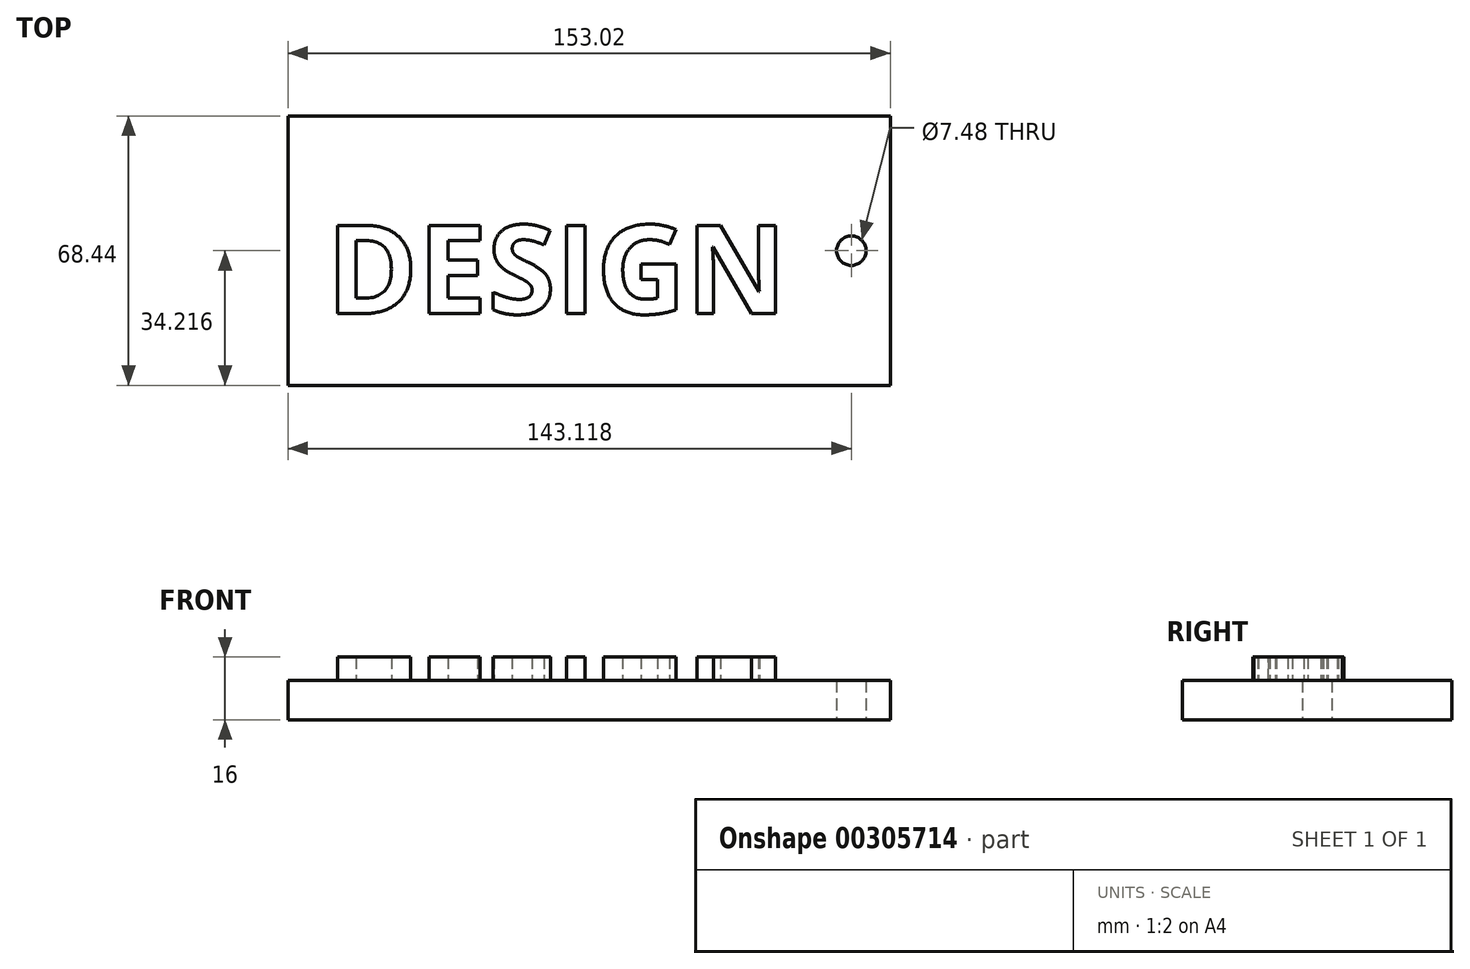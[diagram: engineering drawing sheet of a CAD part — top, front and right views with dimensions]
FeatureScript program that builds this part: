
annotation { "Feature Type Name" : "Feature", "Feature Type Description" : "" }
export const myFeature = defineFeature(function(context is Context, id is Id, definition is map)
    precondition{}
    {
        {
            var Q0;
            Q0=qCreatedBy(makeId("Top.planeOp"),FACE);
            var sketch = newSketch(context, id + "F0", { "sketchPlane" : qUnion([Q0])});
            skLineSegment(sketch, "E0.bottom", {"start": v(-119.97, 50.22) * mm, "end": v(33.05, 50.22) * mm});
            skLineSegment(sketch, "E0.top", {"start": v(-119.97, -18.22) * mm, "end": v(33.05, -18.22) * mm});
            skLineSegment(sketch, "E0.left", {"start": v(-119.97, 50.22) * mm, "end": v(-119.97, -18.22) * mm});
            skLineSegment(sketch, "E0.right", {"start": v(33.05, 50.22) * mm, "end": v(33.05, -18.22) * mm});
            skPoint(sketch, "E1.centerSnap0", {"position": v(33.05, 16) * mm});
            skCircle(sketch, "E2", {"center": v(23.15, 16) * mm, "radius": 3.74 * mm});
            skSolve(sketch);
        }
        {
            var Q0;
            Q0=makeQuery(id+"F0.imprint","IMPRINT",FACE,{"disambiguationData":[TD([[makeQuery(id+"F0.imprint","IMPRINT",EDGE,{"derivedFrom":sQuery(id+"F0.wireOp",EDGE,"E0.bottom")}),-1.0]])]});
            extrude(context, id + "F1", {"entities" : qUnion([Q0]), "depth" : 10 * mm});
        }
        {
            var Q0;
            Q0=makeQuery(id+"F1.opExtrude","CAP_FACE",FACE,{"disambiguationData":[OSD([sQuery(id+"F0.wireOp",EDGE,"E0.bottom"),sQuery(id+"F0.wireOp",EDGE,"E0.top"),sQuery(id+"F0.wireOp",EDGE,"E0.left"),sQuery(id+"F0.wireOp",EDGE,"E0.right")])],"isStart":false});
            var sketch = newSketch(context, id + "F2", { "sketchPlane" : qUnion([Q0])});
            skText(sketch, "E3", { "text": "DESIGN", "fontName": "OpenSans-Bold.ttf"});
            const initialGuessF2  = {"E3": [-0.11021, 0, 1, 0, 0.02262]};
            skSetInitialGuess(sketch, initialGuessF2);
            skSolve(sketch);
        }
        {
            var Q0;
            Q0 = qSketchRegion(id + "F2", true);
            extrude(context, id + "F3", {"entities" : qUnion([Q0]), "operationType" : NewBodyOperationType.ADD, "depth" : 6 * mm});
        }
    });
